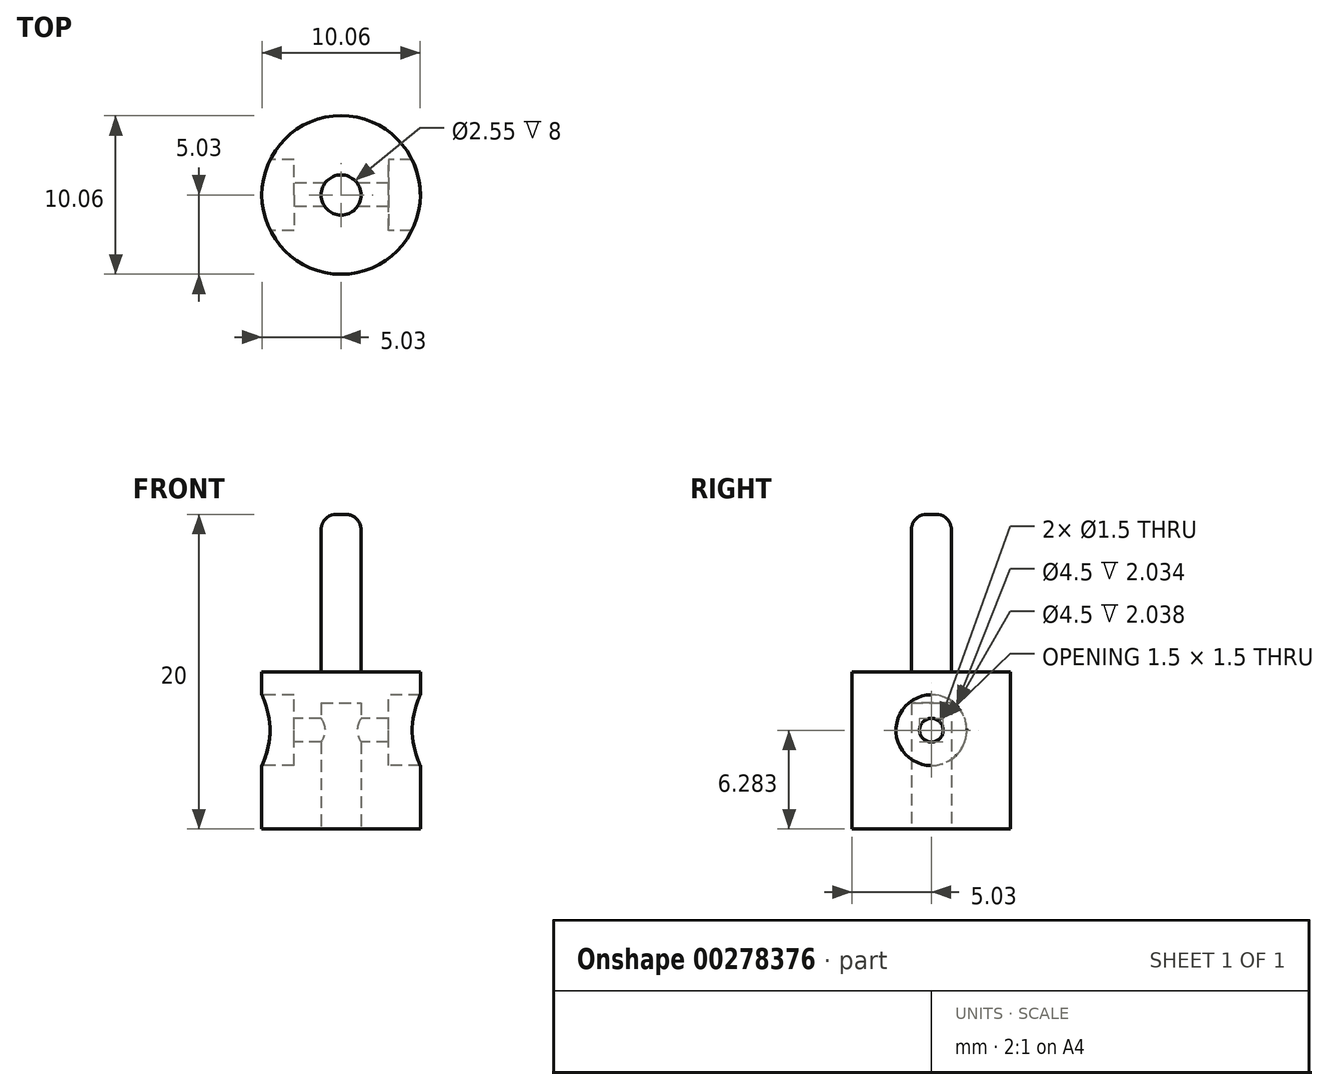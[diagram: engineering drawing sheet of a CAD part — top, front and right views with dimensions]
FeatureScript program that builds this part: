
annotation { "Feature Type Name" : "Feature", "Feature Type Description" : "" }
export const myFeature = defineFeature(function(context is Context, id is Id, definition is map)
    precondition{}
    {
        {
            var Q0;
            Q0=qCreatedBy(makeId("Top.planeOp"),FACE);
            var sketch = newSketch(context, id + "F0", { "sketchPlane" : qUnion([Q0])});
            skPoint(sketch, "E0.middle", {"position": v(0, 0) * mm});
            skCircle(sketch, "E1", {"center": v(0, 0) * mm, "radius": 1.27 * mm});
            skLineSegment(sketch, "E2", {"start": v(0, 5) * mm, "end": v(0, -5) * mm});
            skLineSegment(sketch, "E3", {"start": v(-5, 0) * mm, "end": v(5, 0) * mm});
            skCircle(sketch, "E4", {"center": v(0, 0) * mm, "radius": 5.03 * mm});
            skLineSegment(sketch, "E5", {"start": v(-5, -2.88) * mm, "end": v(-5.08, 3.44) * mm});
            skLineSegment(sketch, "E6", {"start": v(2.88, -5) * mm, "end": v(-2.6, -5.07) * mm});
            skSolve(sketch);
        }
        {
            var Q0;
            Q0=makeQuery(id+"F0.imprint","IMPRINT",FACE,{"disambiguationData":[TD([[makeQuery(id+"F0.imprint","IMPRINT",EDGE,{"derivedFrom":sQuery(id+"F0.wireOp",EDGE,"E1")}),1.0]])]});
            var Q1;
            Q1=makeQuery(id+"F0.imprint","IMPRINT",FACE,{"disambiguationData":[TD([[makeQuery(id+"F0.imprint","IMPRINT",EDGE,{"derivedFrom":sQuery(id+"F0.wireOp",EDGE,"fd2274da-595a-4373-85f8-a78b1814d8c00.MirrorC")}),-1.0]])]});
            var Q2;
            Q2=makeQuery(id+"F0.imprint","IMPRINT",FACE,{"disambiguationData":[TD([[makeQuery(id+"F0.imprint","IMPRINT",EDGE,{"derivedFrom":sQuery(id+"F0.wireOp",EDGE,"48179f1f-f7ea-4e47-a785-d71cd536f9210.MirrorC")}),1.0]])]});
            var Q3;
            Q3=makeQuery(id+"F0.imprint","IMPRINT",FACE,{"disambiguationData":[TD([[makeQuery(id+"F0.imprint","IMPRINT",EDGE,{"derivedFrom":sQuery(id+"F0.wireOp",EDGE,"f465e17f-47d2-4f61-889b-02688481066e0.MirrorC")}),-1.0]])]});
            extrude(context, id + "F1", {"entities" : qUnion([Q0, Q1, Q2, Q3]), "depth" : 10 * mm});
        }
        {
            var Q0;
            Q0=qSketchRegion(id+"F0",true);
            var Q1;
            Q1=makeQuery(id+"F0.imprint","IMPRINT",FACE,{"disambiguationData":[TD([[makeQuery(id+"F0.imprint","IMPRINT",EDGE,{"derivedFrom":sQuery(id+"F0.wireOp",EDGE,"48179f1f-f7ea-4e47-a785-d71cd536f9210.MirrorC")}),1.0]])]});
            var Q2;
            Q2=makeQuery(id+"F0.imprint","IMPRINT",FACE,{"disambiguationData":[TD([[makeQuery(id+"F0.imprint","IMPRINT",EDGE,{"derivedFrom":sQuery(id+"F0.wireOp",EDGE,"fd2274da-595a-4373-85f8-a78b1814d8c00.MirrorC")}),-1.0]])]});
            var Q3;
            Q3=makeQuery(id+"F0.imprint","IMPRINT",FACE,{"disambiguationData":[TD([[makeQuery(id+"F0.imprint","IMPRINT",EDGE,{"derivedFrom":sQuery(id+"F0.wireOp",EDGE,"E1")}),1.0]])]});
            var Q4;
            Q4=makeQuery(id+"F0.imprint","IMPRINT",FACE,{"disambiguationData":[TD([[makeQuery(id+"F0.imprint","IMPRINT",EDGE,{"derivedFrom":sQuery(id+"F0.wireOp",EDGE,"f465e17f-47d2-4f61-889b-02688481066e0.MirrorC")}),-1.0]])]});
            extrude(context, id + "F2", {"entities" : qUnion([Q0, Q1, Q2, Q3, Q4]), "oppositeDirection" : true, "depth" : 10 * mm});
        }
        {
            var Q0;
            Q0=makeQuery(id+"F1.opExtrude","CAP_EDGE",EDGE,{"disambiguationData":[OSD([sQuery(id+"F0.wireOp",EDGE,"E1")])],"isStart":false});
            fillet(context, id + "F3", {"entities" : qUnion([Q0]), "radius" : 1 * mm, "tangentPropagation" : true, "allowEdgeOverflow" : false});
        }
        {
            var Q0;
            Q0=makeQuery(id+"F2.opExtrude","CAP_FACE",FACE,{"disambiguationData":[OSD([sQuery(id+"F0.wireOp",EDGE,"E4")])],"isStart":false});
            var sketch = newSketch(context, id + "F4", { "sketchPlane" : qUnion([Q0])});
            skCircle(sketch, "E7.0", {"center": v(0, 0) * mm, "radius": 1.27 * mm});
            skSolve(sketch);
        }
        {
            var Q0;
            Q0 = qSketchRegion(id + "F4", true);
            extrude(context, id + "F5", {"entities" : qUnion([Q0]), "operationType" : NewBodyOperationType.REMOVE, "oppositeDirection" : true, "depth" : 8 * mm});
        }
        {
            var Q0;
            Q0=qCreatedBy(makeId("Right.planeOp"),FACE);
            var sketch = newSketch(context, id + "F6", { "sketchPlane" : qUnion([Q0])});
            skLineSegment(sketch, "E8", {"start": v(0, 0) * mm, "end": v(0, -10.78) * mm, "construction": true});
            skCircle(sketch, "E9", {"center": v(0, -3.72) * mm, "radius": 0.75 * mm});
            skSolve(sketch);
        }
        {
            var Q0;
            Q0=makeQuery(id+"F6.imprint","IMPRINT",FACE,{"disambiguationData":[TD([[makeQuery(id+"F6.imprint","IMPRINT",EDGE,{"derivedFrom":sQuery(id+"F6.wireOp",EDGE,"E9")}),1.0]])]});
            extrude(context, id + "F7", {"entities" : qUnion([Q0]), "operationType" : NewBodyOperationType.REMOVE, "endBound" : BoundingType.SYMMETRIC, "depth" : 25 * mm});
        }
        {
            var Q0;
            Q0=qCreatedBy(makeId("Right.planeOp"),FACE);
            cPlane(context, id + "F8", {"entities" : qUnion([Q0]), "cplaneType" : CPlaneType.OFFSET, "offset" : 5 * mm, "width" : 150 * mm, "height" : 150 * mm});
        }
        {
            var Q0;
            Q0=qCreatedBy(id+"F8.planeOp",FACE);
            var sketch = newSketch(context, id + "F9", { "sketchPlane" : qUnion([Q0])});
            skCircle(sketch, "E10.0", {"center": v(0, -3.72) * mm, "radius": 0.75 * mm});
            skCircle(sketch, "E11.0", {"center": v(0, -3.72) * mm, "radius": 2.25 * mm});
            skSolve(sketch);
        }
        {
            var Q0;
            Q0 = qSketchRegion(id + "F9", true);
            extrude(context, id + "F10", {"entities" : qUnion([Q0]), "operationType" : NewBodyOperationType.REMOVE, "endBound" : BoundingType.SYMMETRIC, "depth" : 4 * mm});
        }
        {
            var Q0;
            Q0=qCreatedBy(makeId("Right.planeOp"),FACE);
            cPlane(context, id + "F11", {"entities" : qUnion([Q0]), "cplaneType" : CPlaneType.OFFSET, "offset" : 5 * mm, "oppositeDirection" : true, "width" : 150 * mm, "height" : 150 * mm});
        }
        {
            var Q0;
            Q0=qCreatedBy(id+"F11.planeOp",FACE);
            var sketch = newSketch(context, id + "F12", { "sketchPlane" : qUnion([Q0])});
            skCircle(sketch, "E12.0", {"center": v(0, -3.72) * mm, "radius": 0.75 * mm});
            skCircle(sketch, "E13.0", {"center": v(0, -3.72) * mm, "radius": 2.25 * mm});
            skSolve(sketch);
        }
        {
            var Q0;
            Q0 = qSketchRegion(id + "F12", true);
            extrude(context, id + "F13", {"entities" : qUnion([Q0]), "operationType" : NewBodyOperationType.REMOVE, "endBound" : BoundingType.SYMMETRIC, "depth" : 4 * mm});
        }
    });
